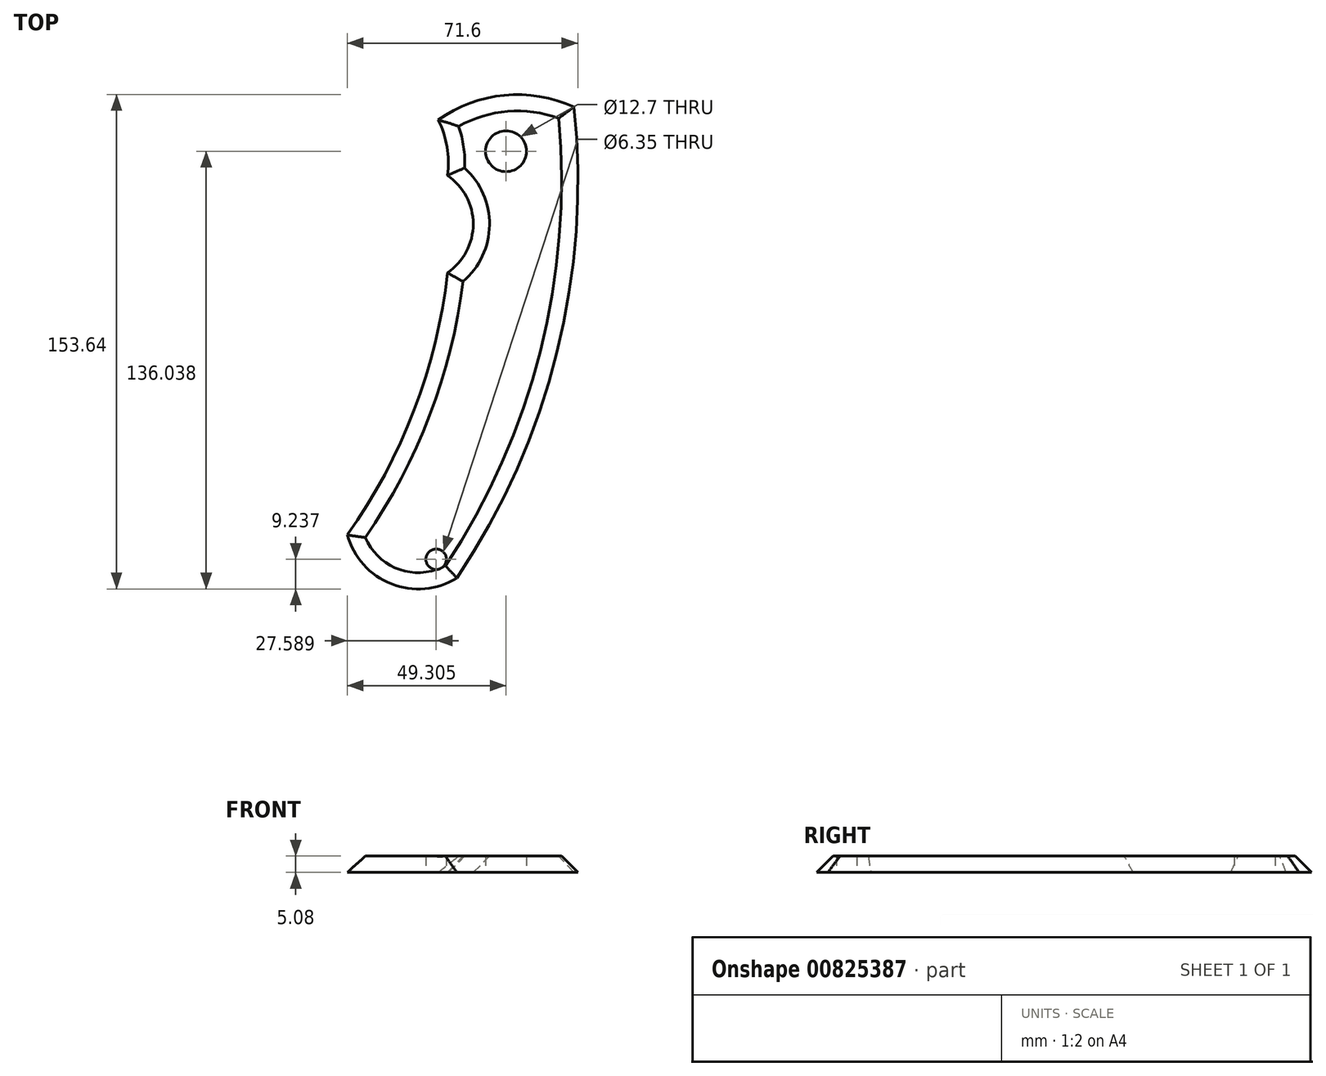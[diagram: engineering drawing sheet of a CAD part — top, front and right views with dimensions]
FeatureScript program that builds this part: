
annotation { "Feature Type Name" : "Feature", "Feature Type Description" : "" }
export const myFeature = defineFeature(function(context is Context, id is Id, definition is map)
    precondition{}
    {
        {
            var Q0;
            Q0=qCreatedBy(makeId("Top.planeOp"),FACE);
            var sketch = newSketch(context, id + "F0", { "sketchPlane" : qUnion([Q0])});
            skArc(sketch, "E0", {"start": v(24.88, 37.68) * mm, "mid": v(3.23, 41.34) * mm, "end": v(-17.31, 33.6) * mm});
            skArc(sketch, "E1", {"start": v(-11.5, -108.67) * mm, "mid": v(19.54, -38.69) * mm, "end": v(24.88, 37.68) * mm});
            skArc(sketch, "E2", {"start": v(-14.4, 16.44) * mm, "mid": v(-14.55, 25.24) * mm, "end": v(-17.31, 33.6) * mm});
            skArc(sketch, "E3", {"start": v(-14.4, -13.82) * mm, "mid": v(-6.43, 1.3) * mm, "end": v(-14.4, 16.44) * mm});
            skArc(sketch, "E4", {"start": v(-45.53, -95.28) * mm, "mid": v(-24.77, -56.54) * mm, "end": v(-14.4, -13.82) * mm});
            skArc(sketch, "E5", {"start": v(-45.53, -95.28) * mm, "mid": v(-31.87, -110.52) * mm, "end": v(-11.5, -108.67) * mm});
            skCircle(sketch, "E6", {"center": v(3.77, 23.93) * mm, "radius": 6.35 * mm});
            skCircle(sketch, "E7", {"center": v(-17.94, -102.87) * mm, "radius": 3.18 * mm});
            skPoint(sketch, "E8", {"position": v(-28.14, -64.73) * mm});
            skPoint(sketch, "E9", {"position": v(6.45, -76.41) * mm});
            skPoint(sketch, "E10", {"position": v(-14.4, 16.44) * mm});
            skPoint(sketch, "E11", {"position": v(-14.4, -13.82) * mm});
            skPoint(sketch, "E12", {"position": v(24.88, 37.68) * mm});
            skPoint(sketch, "E13", {"position": v(-11.5, -108.67) * mm});
            skPoint(sketch, "E14", {"position": v(-45.53, -95.28) * mm});
            skPoint(sketch, "E15", {"position": v(-17.31, 33.6) * mm});
            skPoint(sketch, "E16", {"position": v(3.23, 41.34) * mm});
            skPoint(sketch, "E17", {"position": v(-21.98, -112.05) * mm});
            skSolve(sketch);
        }
        {
            var Q0;
            Q0 = qSketchRegion(id + "F0", true);
            extrude(context, id + "F1", {"entities" : qUnion([Q0]), "depth" : 5.08 * mm, "offsetDistance" : 25.4 * mm});
        }
        {
            var Q0;
            Q0=makeQuery(id+"F1.opExtrude","CAP_EDGE",EDGE,{"disambiguationData":[OSD([sQuery(id+"F0.wireOp",EDGE,"E5")])],"isStart":false});
            var Q1;
            Q1=makeQuery(id+"F1.opExtrude","CAP_EDGE",EDGE,{"disambiguationData":[OSD([sQuery(id+"F0.wireOp",EDGE,"E4")])],"isStart":false});
            var Q2;
            Q2=makeQuery(id+"F1.opExtrude","CAP_EDGE",EDGE,{"disambiguationData":[OSD([sQuery(id+"F0.wireOp",EDGE,"E0")])],"isStart":false});
            var Q3;
            Q3=makeQuery(id+"F1.opExtrude","CAP_EDGE",EDGE,{"disambiguationData":[OSD([sQuery(id+"F0.wireOp",EDGE,"E2")])],"isStart":false});
            var Q4;
            Q4=makeQuery(id+"F1.opExtrude","CAP_EDGE",EDGE,{"disambiguationData":[OSD([sQuery(id+"F0.wireOp",EDGE,"E3")])],"isStart":false});
            var Q5;
            Q5=makeQuery(id+"F1.opExtrude","CAP_EDGE",EDGE,{"disambiguationData":[OSD([sQuery(id+"F0.wireOp",EDGE,"E1")])],"isStart":false});
            chamfer(context, id + "F2", {"entities" : qUnion([Q0, Q1, Q2, Q3, Q4, Q5]), "width" : 5.08 * mm, "tangentPropagation" : true});
        }
    });
